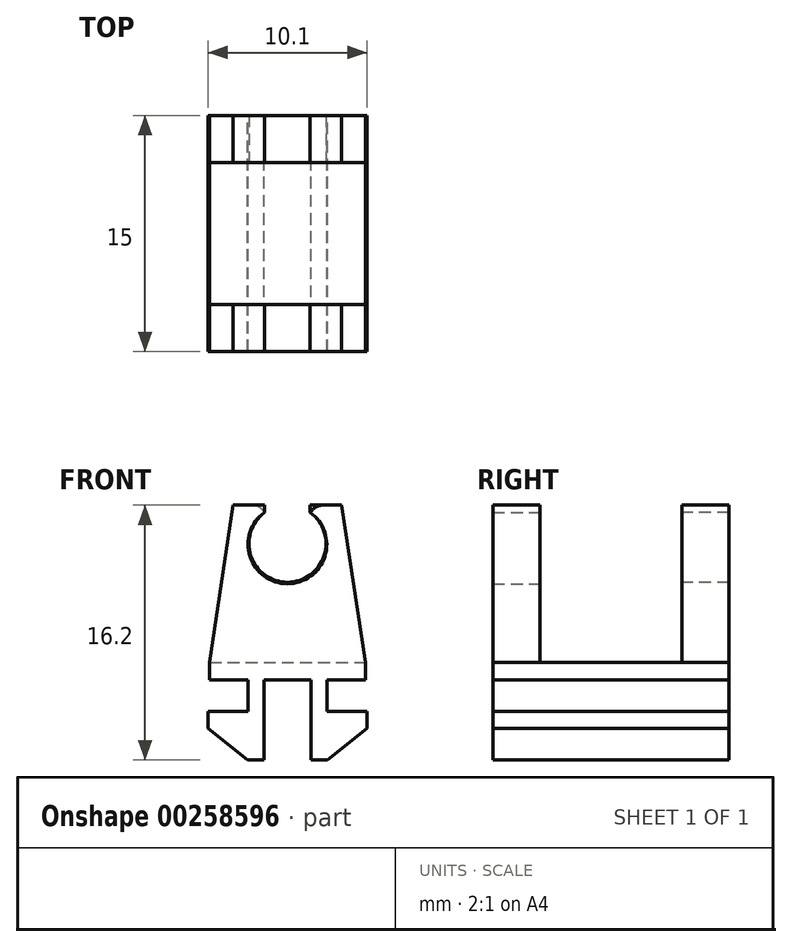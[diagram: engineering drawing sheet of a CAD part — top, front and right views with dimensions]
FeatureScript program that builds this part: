
annotation { "Feature Type Name" : "Feature", "Feature Type Description" : "" }
export const myFeature = defineFeature(function(context is Context, id is Id, definition is map)
    precondition{}
    {
        {
            var Q0;
            Q0=qCreatedBy(makeId("Front.planeOp"),FACE);
            var sketch = newSketch(context, id + "F0", { "sketchPlane" : qUnion([Q0])});
            skLineSegment(sketch, "E0.top", {"start": v(-5.05, 0.55) * mm, "end": v(-2.5, 0.55) * mm});
            skLineSegment(sketch, "E0.left", {"start": v(-5.05, -0.55) * mm, "end": v(-5.05, 0.55) * mm});
            skLineSegment(sketch, "E0.right", {"start": v(5.05, -0.55) * mm, "end": v(5.05, 0.55) * mm});
            skPoint(sketch, "E0.middle", {"position": v(0, 0) * mm});
            skLineSegment(sketch, "E1.top", {"start": v(-2.55, -2.55) * mm, "end": v(-1.5, -2.55) * mm});
            skLineSegment(sketch, "E2", {"start": v(-1.5, -2.55) * mm, "end": v(-2.55, -2.55) * mm});
            skLineSegment(sketch, "E3.MirrorCS", {"start": v(1.5, -2.55) * mm, "end": v(2.55, -2.55) * mm});
            skLineSegment(sketch, "E4", {"start": v(-2.55, -2.55) * mm, "end": v(-5.05, -0.55) * mm});
            skLineSegment(sketch, "E5", {"start": v(2.55, -2.55) * mm, "end": v(5.05, -0.55) * mm});
            skLineSegment(sketch, "E6", {"start": v(0, 0) * mm, "end": v(0, 2.55) * mm});
            skPoint(sketch, "E6.endSnap0", {"position": v(0, 0.55) * mm});
            skLineSegment(sketch, "E7.0", {"start": v(2.5, 0.55) * mm, "end": v(2.5, 2.55) * mm});
            skLineSegment(sketch, "E8.0", {"start": v(-2.5, 0.55) * mm, "end": v(-2.5, 2.55) * mm});
            skLineSegment(sketch, "E9.0", {"start": v(1.5, -2.55) * mm, "end": v(1.5, 2.55) * mm});
            skLineSegment(sketch, "E10.0", {"start": v(-1.5, -2.55) * mm, "end": v(-1.5, 2.55) * mm});
            skPoint(sketch, "E11.orphan", {"position": v(0, -2.55) * mm});
            skLineSegment(sketch, "E12.0", {"start": v(-4.95, 2.55) * mm, "end": v(-2.5, 2.55) * mm});
            skLineSegment(sketch, "E13.trimOffspring", {"start": v(2.5, 0.55) * mm, "end": v(5.05, 0.55) * mm});
            skLineSegment(sketch, "E14.top", {"start": v(-4.95, 3.65) * mm, "end": v(4.95, 3.65) * mm});
            skLineSegment(sketch, "E14.left", {"start": v(-4.95, 2.55) * mm, "end": v(-4.95, 3.65) * mm});
            skLineSegment(sketch, "E14.right", {"start": v(4.95, 2.55) * mm, "end": v(4.95, 3.65) * mm});
            skLineSegment(sketch, "E15.trimOffspring", {"start": v(-1.5, 2.55) * mm, "end": v(1.5, 2.55) * mm});
            skLineSegment(sketch, "E16.trimOffspring", {"start": v(2.5, 2.55) * mm, "end": v(4.95, 2.55) * mm});
            skSolve(sketch);
        }
        {
            var Q0;
            Q0 = qSketchRegion(id + "F0", true);
            extrude(context, id + "F1", {"entities" : qUnion([Q0]), "depth" : 15 * mm});
        }
        {
            var Q0;
            Q0=makeQuery(id+"F1.opExtrude","CAP_FACE",FACE,{"disambiguationData":[OSD([sQuery(id+"F0.wireOp",EDGE,"E0.top"),sQuery(id+"F0.wireOp",EDGE,"E0.left"),sQuery(id+"F0.wireOp",EDGE,"E0.right"),sQuery(id+"F0.wireOp",EDGE,"E2"),sQuery(id+"F0.wireOp",EDGE,"E4"),sQuery(id+"F0.wireOp",EDGE,"E5"),sQuery(id+"F0.wireOp",EDGE,"E7.0"),sQuery(id+"F0.wireOp",EDGE,"E8.0"),sQuery(id+"F0.wireOp",EDGE,"E9.0"),sQuery(id+"F0.wireOp",EDGE,"E10.0"),sQuery(id+"F0.wireOp",EDGE,"E3.MirrorCS"),sQuery(id+"F0.wireOp",EDGE,"E13.trimOffspring"),sQuery(id+"F0.wireOp",EDGE,"E12.0"),sQuery(id+"F0.wireOp",EDGE,"E14.top"),sQuery(id+"F0.wireOp",EDGE,"E14.left"),sQuery(id+"F0.wireOp",EDGE,"E14.right"),sQuery(id+"F0.wireOp",EDGE,"E16.trimOffspring"),sQuery(id+"F0.wireOp",EDGE,"E15.trimOffspring")])],"isStart":false});
            var sketch = newSketch(context, id + "F2", { "sketchPlane" : qUnion([Q0])});
            skLineSegment(sketch, "E17.bottom", {"start": v(-4.08, 3.65) * mm, "end": v(-0.75, 3.65) * mm});
            skLineSegment(sketch, "E18.top", {"start": v(-0.25, 8.43) * mm, "end": v(0.25, 8.43) * mm});
            skLineSegment(sketch, "E18.left", {"start": v(-0.75, 6.85) * mm, "end": v(-0.75, 6.93) * mm});
            skLineSegment(sketch, "E18.right", {"start": v(0.75, 6.83) * mm, "end": v(0.75, 6.93) * mm});
            skPoint(sketch, "E18.middle", {"position": v(0, 7.68) * mm});
            skLineSegment(sketch, "E19", {"start": v(-0.75, 7.68) * mm, "end": v(-4.95, 3.65) * mm});
            skLineSegment(sketch, "E20", {"start": v(0.75, 7.68) * mm, "end": v(4.76, 3.65) * mm});
            skPoint(sketch, "E17.left.end.orphan", {"position": v(-4.95, 7.68) * mm});
            skPoint(sketch, "E17.right.end.orphan", {"position": v(4.95, 7.68) * mm});
            skPoint(sketch, "E21.endSnap0", {"position": v(3.73, 2.55) * mm});
            skLineSegment(sketch, "E22.0", {"start": v(-0.75, 6.85) * mm, "end": v(-4.08, 3.65) * mm});
            skLineSegment(sketch, "E23.0", {"start": v(0.75, 6.83) * mm, "end": v(3.92, 3.65) * mm});
            skPoint(sketch, "E24.visualSharp", {"position": v(-0.75, 8.43) * mm});
            skArc(sketch, "E24.filletArc", {"start": v(-0.25, 8.43) * mm, "mid": v(-0.6, 8.28) * mm, "end": v(-0.75, 7.93) * mm});
            skPoint(sketch, "E25.visualSharp", {"position": v(0.75, 8.43) * mm});
            skArc(sketch, "E25.filletArc", {"start": v(0.75, 7.93) * mm, "mid": v(0.6, 8.28) * mm, "end": v(0.25, 8.43) * mm});
            skLineSegment(sketch, "E26.trimOffspring", {"start": v(-0.75, 7.68) * mm, "end": v(-0.75, 7.93) * mm});
            skLineSegment(sketch, "E27.trimOffspring", {"start": v(0.75, 7.68) * mm, "end": v(0.75, 7.93) * mm});
            skLineSegment(sketch, "E28", {"start": v(-0.75, 6.85) * mm, "end": v(-0.75, 3.65) * mm});
            skLineSegment(sketch, "E29", {"start": v(0.75, 6.93) * mm, "end": v(0.75, 3.65) * mm});
            skLineSegment(sketch, "E30.trimOffspring", {"start": v(0.75, 3.65) * mm, "end": v(3.92, 3.65) * mm});
            skSolve(sketch);
        }
        {
            var Q0;
            Q0=makeQuery(id+"F2.imprint","IMPRINT",FACE,{"disambiguationData":[TD([[makeQuery(id+"F2.imprint","IMPRINT",EDGE,{"derivedFrom":sQuery(id+"F2.wireOp",EDGE,"E18.top")}),-1.0]])]});
            extrude(context, id + "F3", {"entities" : qUnion([Q0]), "oppositeDirection" : true, "depth" : 25 * mm});
        }
        {
            var Q0;
            Q0=makeQuery(id+"F3.opExtrude","SWEPT_FACE",FACE,{"disambiguationData":[OSD([sQuery(id+"F2.wireOp",EDGE,"E19")])]});
            var sketch = newSketch(context, id + "F4", { "sketchPlane" : qUnion([Q0])});
            skLineSegment(sketch, "E31.bottom", {"start": v(-1.05, 8.5) * mm, "end": v(4.77, 8.5) * mm});
            skLineSegment(sketch, "E31.top", {"start": v(-1.05, -13.5) * mm, "end": v(4.77, -13.5) * mm});
            skLineSegment(sketch, "E31.left", {"start": v(-1.05, 8.5) * mm, "end": v(-1.05, -13.5) * mm});
            skLineSegment(sketch, "E31.right", {"start": v(4.77, 8.5) * mm, "end": v(4.77, -13.5) * mm});
            skSolve(sketch);
        }
        {
            var Q0;
            Q0 = qSketchRegion(id + "F4", true);
            extrude(context, id + "F5", {"entities" : qUnion([Q0]), "operationType" : NewBodyOperationType.REMOVE, "endBound" : BoundingType.UP_TO_NEXT, "oppositeDirection" : true, "depth" : 25 * mm});
        }
        {
            var Q0;
            Q0=makeQuery(id+"F3.opExtrude","SWEPT_BODY",BODY,{"disambiguationData":[OSD([sQuery(id+"F0.wireOp",EDGE,"E14.top"),sQuery(id+"F2.wireOp",EDGE,"E18.top"),sQuery(id+"F2.wireOp",EDGE,"E18.right"),sQuery(id+"F2.wireOp",EDGE,"E19"),sQuery(id+"F2.wireOp",EDGE,"E20"),sQuery(id+"F2.wireOp",EDGE,"E22.0"),sQuery(id+"F2.wireOp",EDGE,"E23.0"),sQuery(id+"F2.wireOp",EDGE,"E24.filletArc"),sQuery(id+"F2.wireOp",EDGE,"E25.filletArc"),sQuery(id+"F2.wireOp",EDGE,"E26.trimOffspring"),sQuery(id+"F2.wireOp",EDGE,"E27.trimOffspring"),sQuery(id+"F2.wireOp",EDGE,"E28"),sQuery(id+"F2.wireOp",EDGE,"E29")])]});
            deleteBodies(context, id + "F6", {"entities" : qUnion([Q0])});
        }
        {
            var Q0;
            Q0=makeQuery(id+"F1.opExtrude","SWEPT_FACE",FACE,{"disambiguationData":[OSD([sQuery(id+"F0.wireOp",EDGE,"E14.top")])]});
            var sketch = newSketch(context, id + "F7", { "sketchPlane" : qUnion([Q0])});
            skLineSegment(sketch, "E32.bottom", {"start": v(-4.95, -15) * mm, "end": v(4.95, -15) * mm});
            skLineSegment(sketch, "E32.top", {"start": v(-4.95, -12) * mm, "end": v(4.95, -12) * mm});
            skLineSegment(sketch, "E32.left", {"start": v(-4.95, -15) * mm, "end": v(-4.95, -12) * mm});
            skLineSegment(sketch, "E32.right", {"start": v(4.95, -15) * mm, "end": v(4.95, -12) * mm});
            skLineSegment(sketch, "E33.bottom", {"start": v(4.95, 0) * mm, "end": v(-4.95, 0) * mm});
            skLineSegment(sketch, "E33.top", {"start": v(4.95, -3) * mm, "end": v(-4.95, -3) * mm});
            skLineSegment(sketch, "E33.left", {"start": v(4.95, 0) * mm, "end": v(4.95, -3) * mm});
            skLineSegment(sketch, "E33.right", {"start": v(-4.95, 0) * mm, "end": v(-4.95, -3) * mm});
            skSolve(sketch);
        }
        {
            var Q0;
            Q0 = qSketchRegion(id + "F7", true);
            extrude(context, id + "F8", {"entities" : qUnion([Q0]), "operationType" : NewBodyOperationType.ADD, "depth" : 10 * mm});
        }
        {
            var Q0;
            Q0=makeQuery(id+"F8.opExtrude","SWEPT_FACE",FACE,{"disambiguationData":[OSD([sQuery(id+"F7.wireOp",EDGE,"E33.top")])]});
            var sketch = newSketch(context, id + "F9", { "sketchPlane" : qUnion([Q0])});
            skArc(sketch, "E34", {"start": v(-1.45, 13.17) * mm, "mid": v(0, 8.75) * mm, "end": v(1.45, 13.17) * mm});
            skPoint(sketch, "E34.centerSnap0", {"position": v(0, 13.65) * mm});
            skLineSegment(sketch, "E35.0", {"start": v(-1.45, 13.65) * mm, "end": v(-1.45, 13.17) * mm});
            skLineSegment(sketch, "E36.0", {"start": v(1.45, 13.65) * mm, "end": v(1.45, 13.17) * mm});
            skLineSegment(sketch, "E37.0", {"start": v(-3.45, 13.65) * mm, "end": v(-3.45, 3.65) * mm, "construction": true});
            skLineSegment(sketch, "E38.0", {"start": v(3.45, 13.65) * mm, "end": v(3.45, 3.65) * mm, "construction": true});
            skLineSegment(sketch, "E39", {"start": v(-3.45, 13.65) * mm, "end": v(-4.95, 3.65) * mm});
            skLineSegment(sketch, "E40", {"start": v(3.45, 13.65) * mm, "end": v(4.95, 3.65) * mm});
            skLineSegment(sketch, "E41", {"start": v(-1.45, 13.65) * mm, "end": v(-3.45, 13.65) * mm});
            skLineSegment(sketch, "E42", {"start": v(1.45, 13.65) * mm, "end": v(3.45, 13.65) * mm});
            skLineSegment(sketch, "E43", {"start": v(-1.45, 13.65) * mm, "end": v(1.45, 13.65) * mm});
            skLineSegment(sketch, "E44", {"start": v(-3.45, 13.65) * mm, "end": v(-4.95, 13.65) * mm});
            skLineSegment(sketch, "E45", {"start": v(-4.95, 13.65) * mm, "end": v(-4.95, 3.65) * mm});
            skLineSegment(sketch, "E46", {"start": v(4.95, 3.65) * mm, "end": v(4.95, 13.65) * mm});
            skLineSegment(sketch, "E47", {"start": v(4.95, 13.65) * mm, "end": v(3.45, 13.65) * mm});
            skSolve(sketch);
        }
        {
            var Q0;
            Q0 = qSketchRegion(id + "F9", true);
            extrude(context, id + "F10", {"entities" : qUnion([Q0]), "operationType" : NewBodyOperationType.REMOVE, "endBound" : BoundingType.UP_TO_NEXT, "oppositeDirection" : true, "depth" : 25 * mm});
        }
        {
            var Q0;
            Q0=makeQuery(id+"F8.opExtrude","SWEPT_FACE",FACE,{"disambiguationData":[OSD([sQuery(id+"F7.wireOp",EDGE,"E32.top")])]});
            var sketch = newSketch(context, id + "F11", { "sketchPlane" : qUnion([Q0])});
            skArc(sketch, "E48", {"start": v(-1.45, 13.19) * mm, "mid": v(0, 8.65) * mm, "end": v(1.45, 13.19) * mm});
            skPoint(sketch, "E48.centerSnap0", {"position": v(0, 13.65) * mm});
            skLineSegment(sketch, "E49.0", {"start": v(1.45, 13.65) * mm, "end": v(1.45, 13.19) * mm});
            skLineSegment(sketch, "E50.0", {"start": v(3.45, 13.65) * mm, "end": v(3.45, 3.65) * mm});
            skLineSegment(sketch, "E51.0", {"start": v(-1.45, 13.65) * mm, "end": v(-1.45, 13.19) * mm});
            skLineSegment(sketch, "E52.0", {"start": v(-3.45, 13.65) * mm, "end": v(-3.45, 3.65) * mm});
            skLineSegment(sketch, "E53", {"start": v(3.45, 13.65) * mm, "end": v(4.95, 3.65) * mm});
            skLineSegment(sketch, "E54", {"start": v(4.95, 3.65) * mm, "end": v(4.95, 13.65) * mm});
            skLineSegment(sketch, "E55", {"start": v(4.95, 13.65) * mm, "end": v(3.45, 13.65) * mm});
            skLineSegment(sketch, "E56", {"start": v(-3.45, 13.65) * mm, "end": v(-4.95, 13.65) * mm});
            skLineSegment(sketch, "E57", {"start": v(-4.95, 13.65) * mm, "end": v(-4.95, 3.65) * mm});
            skLineSegment(sketch, "E58", {"start": v(-4.95, 3.65) * mm, "end": v(-3.45, 13.65) * mm});
            skLineSegment(sketch, "E59", {"start": v(-1.45, 13.65) * mm, "end": v(1.45, 13.65) * mm});
            skSolve(sketch);
        }
        {
            var Q0;
            Q0 = qSketchRegion(id + "F11", true);
            extrude(context, id + "F12", {"entities" : qUnion([Q0]), "operationType" : NewBodyOperationType.REMOVE, "endBound" : BoundingType.UP_TO_NEXT, "oppositeDirection" : true, "depth" : 25 * mm});
        }
        {
            var Q0;
            Q0=makeQuery(id+"F10.boolean.opBoolean","COPY",EDGE,{"derivedFrom":makeQuery(id+"F10.opExtrude","SWEPT_EDGE",EDGE,{"disambiguationData":[OSD([sQuery(id+"F9.wireOp",EDGE,"E36.0"),sQuery(id+"F9.wireOp",EDGE,"E42"),sQuery(id+"F9.wireOp",EDGE,"E43")])]})});
            var Q1;
            Q1=makeQuery(id+"F12.boolean.opBoolean","COPY",EDGE,{"derivedFrom":makeQuery(id+"F12.opExtrude","SWEPT_EDGE",EDGE,{"disambiguationData":[OSD([sQuery(id+"F7.wireOp",EDGE,"E32.top"),sQuery(id+"F11.wireOp",EDGE,"E51.0"),sQuery(id+"F11.wireOp",EDGE,"E59")])]})});
            var Q2;
            Q2=makeQuery(id+"F12.boolean.opBoolean","COPY",EDGE,{"derivedFrom":makeQuery(id+"F12.opExtrude","SWEPT_EDGE",EDGE,{"disambiguationData":[OSD([sQuery(id+"F7.wireOp",EDGE,"E32.top"),sQuery(id+"F11.wireOp",EDGE,"E49.0"),sQuery(id+"F11.wireOp",EDGE,"E59")])]})});
            var Q3;
            Q3=makeQuery(id+"F10.boolean.opBoolean","COPY",EDGE,{"derivedFrom":makeQuery(id+"F10.opExtrude","SWEPT_EDGE",EDGE,{"disambiguationData":[OSD([sQuery(id+"F9.wireOp",EDGE,"E35.0"),sQuery(id+"F9.wireOp",EDGE,"E41"),sQuery(id+"F9.wireOp",EDGE,"E43")])]})});
            fillet(context, id + "F13", {"entities" : qUnion([Q0, Q1, Q2, Q3]), "radius" : 1 * mm, "tangentPropagation" : true, "allowEdgeOverflow" : false});
        }
    });
